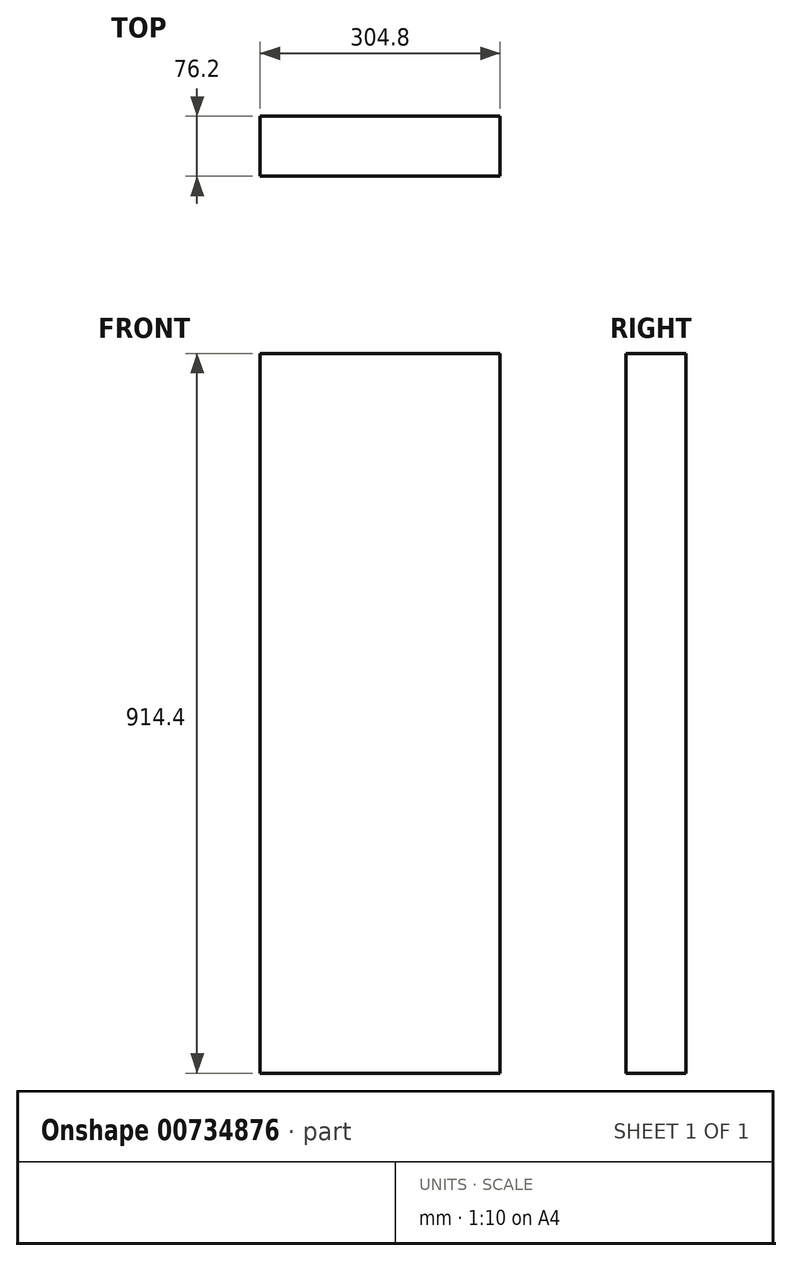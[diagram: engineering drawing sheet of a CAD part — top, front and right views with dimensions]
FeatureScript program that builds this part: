
annotation { "Feature Type Name" : "Feature", "Feature Type Description" : "" }
export const myFeature = defineFeature(function(context is Context, id is Id, definition is map)
    precondition{}
    {
        {
            var Q0;
            Q0=qCreatedBy(makeId("Front.planeOp"),FACE);
            var sketch = newSketch(context, id + "F0", { "sketchPlane" : qUnion([Q0])});
            skLineSegment(sketch, "E0.bottom", {"start": v(187.41, 457.2) * mm, "end": v(-117.39, 457.2) * mm});
            skLineSegment(sketch, "E0.top", {"start": v(187.41, -457.2) * mm, "end": v(-117.39, -457.2) * mm});
            skLineSegment(sketch, "E0.left", {"start": v(187.41, 457.2) * mm, "end": v(187.41, -457.2) * mm});
            skLineSegment(sketch, "E0.right", {"start": v(-117.39, 457.2) * mm, "end": v(-117.39, -457.2) * mm});
            skPoint(sketch, "E0.middle", {"position": v(35.01, 0) * mm});
            skSolve(sketch);
        }
        {
            var Q0;
            Q0=makeQuery(id+"F0.imprint","IMPRINT",FACE,{"disambiguationData":[TD([[makeQuery(id+"F0.imprint","IMPRINT",EDGE,{"derivedFrom":sQuery(id+"F0.wireOp",EDGE,"E0.bottom")}),1.0]])]});
            extrude(context, id + "F1", {"entities" : qUnion([Q0]), "depth" : 76.2 * mm, "offsetDistance" : 25.4 * mm});
        }
    });
